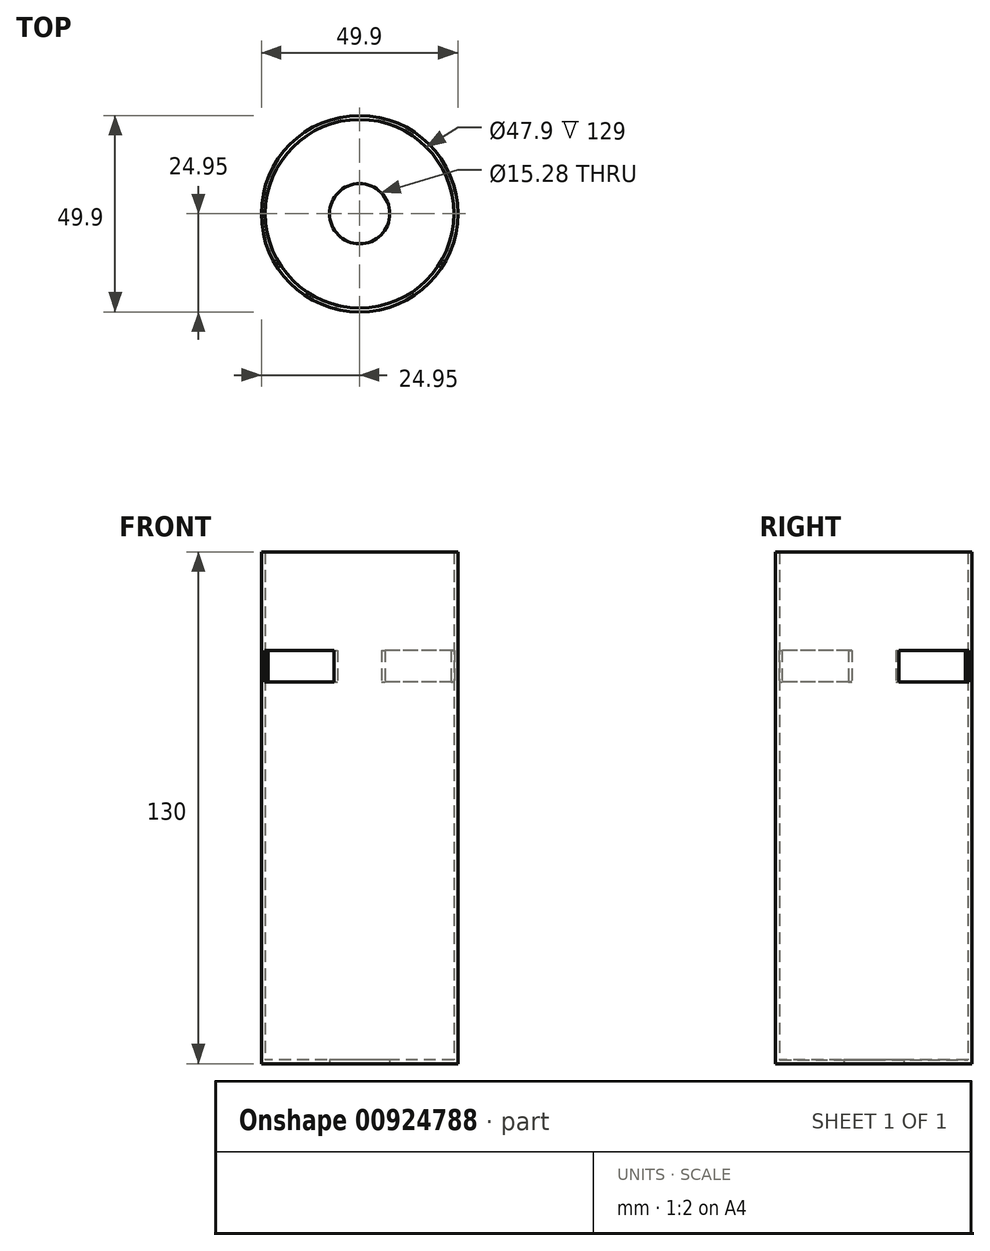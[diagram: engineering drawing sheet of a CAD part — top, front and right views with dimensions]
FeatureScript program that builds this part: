
annotation { "Feature Type Name" : "Feature", "Feature Type Description" : "" }
export const myFeature = defineFeature(function(context is Context, id is Id, definition is map)
    precondition{}
    {
        {
            var Q0;
            Q0=qCreatedBy(makeId("Top.planeOp"),FACE);
            var sketch = newSketch(context, id + "F0", { "sketchPlane" : qUnion([Q0])});
            skCircle(sketch, "E0", {"center": v(0, 0) * mm, "radius": 24.95 * mm});
            skLineSegment(sketch, "E1", {"start": v(0, 0) * mm, "end": v(24.95, 0) * mm, "construction": true});
            skLineSegment(sketch, "E2", {"start": v(0, 0) * mm, "end": v(17.64, 17.64) * mm, "construction": true});
            skSolve(sketch);
        }
        {
            var Q0;
            Q0 = qSketchRegion(id + "F0", true);
            extrude(context, id + "F1", {"entities" : qUnion([Q0]), "depth" : 130 * mm, "offsetDistance" : 25 * mm});
        }
        {
            var Q0;
            Q0=makeQuery(id+"F1.opExtrude","CAP_FACE",FACE,{"disambiguationData":[OSD([sQuery(id+"F0.wireOp",EDGE,"E0")])],"isStart":false});
            shell(context, id + "F2", {"entities" : qUnion([Q0]), "thickness" : mm});
        }
        {
            var Q0;
            Q0=qCreatedBy(makeId("Top.planeOp"),FACE);
            var sketch = newSketch(context, id + "F3", { "sketchPlane" : qUnion([Q0])});
            skCircle(sketch, "E3", {"center": v(0, 0) * mm, "radius": 7.64 * mm});
            skSolve(sketch);
        }
        {
            var Q0;
            Q0 = qSketchRegion(id + "F3", true);
            var Q1;
            {var subQ0=sQuery(id+"F0.wireOp",EDGE,"E0");Q1=makeQuery(id+"F2.opShell","OFFSET_FACE",FACE,{"disambiguationData":[OSD([subQ0]),TDD([makeQuery(id+"F1.opExtrude","CAP_FACE",FACE,{"disambiguationData":[OSD([subQ0])],"isStart":true})])]});}
            extrude(context, id + "F4", {"entities" : qUnion([Q0]), "operationType" : NewBodyOperationType.REMOVE, "endBound" : BoundingType.UP_TO_SURFACE, "depth" : 25 * mm, "endBoundEntityFace" : qUnion([Q1]), "offsetDistance" : 25 * mm});
        }
        {
            var Q0;
            Q0=sQuery(id+"F0.wireOp",EDGE,"E2");
            cPlane(context, id + "F5", {"entities" : qUnion([Q0]), "cplaneType" : CPlaneType.LINE_ANGLE, "offset" : 25 * mm, "angle" : 90 * degree, "width" : 150 * mm, "height" : 150 * mm});
        }
        {
            var Q0;
            Q0=qCreatedBy(id+"F5.planeOp",FACE);
            var sketch = newSketch(context, id + "F6", { "sketchPlane" : qUnion([Q0])});
            skLineSegment(sketch, "E4.bottom", {"start": v(-41.63, 105) * mm, "end": v(36.37, 105) * mm});
            skLineSegment(sketch, "E4.top", {"start": v(-41.63, 97) * mm, "end": v(36.37, 97) * mm});
            skLineSegment(sketch, "E4.left", {"start": v(-41.63, 105) * mm, "end": v(-41.63, 97) * mm});
            skLineSegment(sketch, "E4.right", {"start": v(36.37, 105) * mm, "end": v(36.37, 97) * mm});
            skLineSegment(sketch, "E5", {"start": v(0, 97) * mm, "end": v(0, 0) * mm, "construction": true});
            skLineSegment(sketch, "E6", {"start": v(0, 0) * mm, "end": v(0, 97) * mm, "construction": true});
            skSolve(sketch);
        }
        {
            var Q0;
            Q0 = qSketchRegion(id + "F6", true);
            extrude(context, id + "F7", {"entities" : qUnion([Q0]), "operationType" : NewBodyOperationType.REMOVE, "endBound" : BoundingType.SYMMETRIC, "depth" : 25 * mm, "offsetDistance" : 25 * mm});
        }
    });
